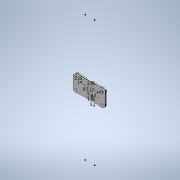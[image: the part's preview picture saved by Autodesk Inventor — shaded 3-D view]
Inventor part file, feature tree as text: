
AUTODESK INVENTOR PART (.ipt)
format: ipt  version: 2022 (Build 260153070, 153G)  size: 163,328 bytes
history: native  units: mm
features: extrude x2, sketch x1
ambient origin geometry x8: Origin, YZ Plane, XZ Plane, XY Plane, X Axis, Y Axis, Z Axis, Center Point
bodies: Solid1 (feature_tree)
feature tree (3):
  sketch  "Sketch1"  dims[d0=1.9mm d1=1.9mm d2=12.0mm d3=1.95mm d4=1.95mm d5=5.0mm d6=5.0mm d7=2.7mm d8=14.0mm d9=14.0mm d10=1.25mm d11=8.5mm d12=8.5mm d13=1.5mm d14=0.0mm d15=1.5mm d16=0.0mm]
  extrude  "Extrusion1"  Depth=1.5mm
  extrude  "Extrusion2"  Depth=1.5mm
